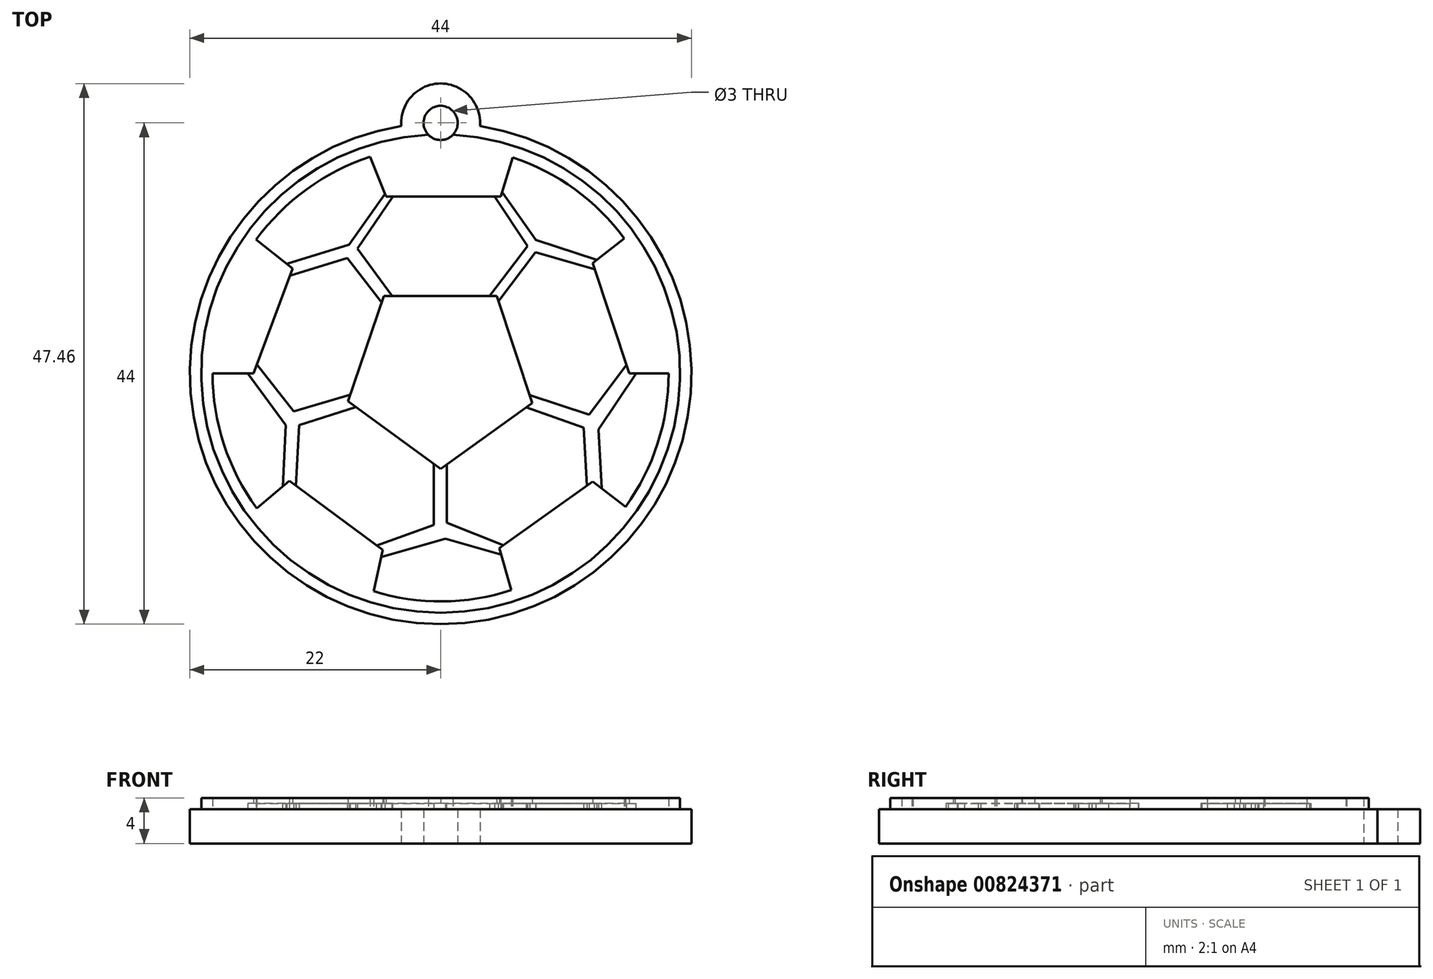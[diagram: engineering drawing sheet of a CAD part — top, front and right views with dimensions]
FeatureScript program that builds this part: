
annotation { "Feature Type Name" : "Feature", "Feature Type Description" : "" }
export const myFeature = defineFeature(function(context is Context, id is Id, definition is map)
    precondition{}
    {
        {
            var Q0;
            Q0=qCreatedBy(makeId("Top.planeOp"),FACE);
            var sketch = newSketch(context, id + "F0", { "sketchPlane" : qUnion([Q0])});
            skArc(sketch, "E0", {"start": v(-3.45, 21.73) * mm, "mid": v(0, -22) * mm, "end": v(3.45, 21.73) * mm});
            skPoint(sketch, "E1.start.orphan", {"position": v(0, -14.87) * mm});
            skCircle(sketch, "E2", {"center": v(0, 22) * mm, "radius": 1.5 * mm});
            skArc(sketch, "E3", {"start": v(3.45, 21.73) * mm, "mid": v(0, 25.46) * mm, "end": v(-3.45, 21.73) * mm});
            skSolve(sketch);
        }
        {
            var Q0;
            Q0=makeQuery(id+"F0.imprint","IMPRINT",FACE,{"disambiguationData":[TD([[makeQuery(id+"F0.imprint","IMPRINT",EDGE,{"derivedFrom":sQuery(id+"F0.wireOp",EDGE,"E0")}),1.0]])]});
            extrude(context, id + "F1", {"entities" : qUnion([Q0]), "depth" : 3 * mm, "offsetDistance" : 25 * mm});
        }
        {
            var Q0;
            Q0=makeQuery(id+"F1.opExtrude","CAP_FACE",FACE,{"disambiguationData":[OSD([sQuery(id+"F0.wireOp",EDGE,"E0")])],"isStart":false});
            var sketch = newSketch(context, id + "F2", { "sketchPlane" : qUnion([Q0])});
            skArc(sketch, "E4", {"start": v(-20, 0) * mm, "mid": v(-19, -6.22) * mm, "end": v(-16.13, -11.83) * mm});
            skLineSegment(sketch, "E5", {"start": v(-6.18, 19.02) * mm, "end": v(-4.8, 15.53) * mm});
            skLineSegment(sketch, "E6", {"start": v(-4.8, 15.53) * mm, "end": v(5.27, 15.53) * mm});
            skLineSegment(sketch, "E7", {"start": v(5.27, 15.53) * mm, "end": v(6.34, 18.97) * mm});
            skLineSegment(sketch, "E8", {"start": v(16.1, 11.85) * mm, "end": v(13.33, 9.69) * mm});
            skLineSegment(sketch, "E9", {"start": v(13.33, 9.69) * mm, "end": v(16.54, 0) * mm});
            skLineSegment(sketch, "E10", {"start": v(16.54, 0) * mm, "end": v(20, 0) * mm});
            skLineSegment(sketch, "E11", {"start": v(-16.18, 11.75) * mm, "end": v(-13, 9.23) * mm});
            skLineSegment(sketch, "E12", {"start": v(-13, 9.23) * mm, "end": v(-16.43, 0) * mm});
            skLineSegment(sketch, "E13", {"start": v(-16.43, 0) * mm, "end": v(-20, 0) * mm});
            skLineSegment(sketch, "E14", {"start": v(-16.13, -11.83) * mm, "end": v(-13.28, -9.43) * mm});
            skLineSegment(sketch, "E15", {"start": v(-13.28, -9.43) * mm, "end": v(-5.1, -15.5) * mm});
            skLineSegment(sketch, "E16", {"start": v(-5.1, -15.5) * mm, "end": v(-5.89, -19.11) * mm});
            skLineSegment(sketch, "E17", {"start": v(6.2, -19.02) * mm, "end": v(5.15, -15.32) * mm});
            skLineSegment(sketch, "E18", {"start": v(5.15, -15.32) * mm, "end": v(13.33, -9.48) * mm});
            skLineSegment(sketch, "E19", {"start": v(13.33, -9.48) * mm, "end": v(16.23, -11.69) * mm});
            skLineSegment(sketch, "E20", {"start": v(-5, 6.8) * mm, "end": v(4.92, 6.8) * mm});
            skLineSegment(sketch, "E21", {"start": v(4.92, 6.8) * mm, "end": v(8.05, -2.58) * mm});
            skLineSegment(sketch, "E22", {"start": v(8.05, -2.58) * mm, "end": v(0, -8.36) * mm});
            skLineSegment(sketch, "E23", {"start": v(0, -8.36) * mm, "end": v(-8.12, -2.44) * mm});
            skLineSegment(sketch, "E24", {"start": v(-8.12, -2.44) * mm, "end": v(-5, 6.8) * mm});
            skCircle(sketch, "E25.0", {"center": v(0, 0) * mm, "radius": 21 * mm});
            skArc(sketch, "E26.trimOffspring", {"start": v(-6.18, 19.02) * mm, "mid": v(-11.76, 16.18) * mm, "end": v(-16.18, 11.75) * mm});
            skArc(sketch, "E27.trimOffspring", {"start": v(16.1, 11.85) * mm, "mid": v(11.77, 16.17) * mm, "end": v(6.34, 18.97) * mm});
            skLineSegment(sketch, "E28.trimOffspring", {"start": v(21, 0) * mm, "end": v(21.06, 0) * mm});
            skArc(sketch, "E29.trimOffspring", {"start": v(16.23, -11.69) * mm, "mid": v(19.03, -6.14) * mm, "end": v(20, 0) * mm});
            skArc(sketch, "E30.trimOffspring", {"start": v(-5.89, -19.11) * mm, "mid": v(0.16, -20) * mm, "end": v(6.2, -19.02) * mm});
            skSolve(sketch);
        }
        {
            var Q0;
            Q0=makeQuery(id+"F2.imprint","IMPRINT",FACE,{"disambiguationData":[TD([[makeQuery(id+"F2.imprint","IMPRINT",EDGE,{"derivedFrom":sQuery(id+"F2.wireOp",EDGE,"E20")}),-1.0]])]});
            var Q1;
            Q1=makeQuery(id+"F2.imprint","IMPRINT",FACE,{"disambiguationData":[TD([[makeQuery(id+"F2.imprint","IMPRINT",EDGE,{"derivedFrom":sQuery(id+"F2.wireOp",EDGE,"E4")}),-1.0]])]});
            extrude(context, id + "F3", {"entities" : qUnion([Q0, Q1]), "depth" : 1 * mm, "offsetDistance" : 25 * mm});
        }
        {
            var Q0;
            Q0=makeQuery(id+"F1.opExtrude","CAP_FACE",FACE,{"disambiguationData":[OSD([sQuery(id+"F0.wireOp",EDGE,"E0")])],"isStart":false});
            var sketch = newSketch(context, id + "F4", { "sketchPlane" : qUnion([Q0])});
            skLineSegment(sketch, "E31", {"start": v(-4.64, 16.12) * mm, "end": v(-8.04, 11.32) * mm});
            skLineSegment(sketch, "E32", {"start": v(-8.04, 11.32) * mm, "end": v(-13.96, 9.48) * mm});
            skLineSegment(sketch, "E33", {"start": v(-13.96, 9.48) * mm, "end": v(-13.3, 8.57) * mm});
            skLineSegment(sketch, "E34", {"start": v(-13.3, 8.57) * mm, "end": v(-8.2, 10.13) * mm});
            skLineSegment(sketch, "E35", {"start": v(-8.2, 10.13) * mm, "end": v(-5.02, 6.01) * mm});
            skLineSegment(sketch, "E36", {"start": v(-5.02, 6.01) * mm, "end": v(-4.17, 6.67) * mm});
            skLineSegment(sketch, "E37", {"start": v(-4.17, 6.67) * mm, "end": v(-7.31, 10.98) * mm});
            skLineSegment(sketch, "E38", {"start": v(-7.31, 10.98) * mm, "end": v(-3.97, 15.86) * mm});
            skLineSegment(sketch, "E39", {"start": v(-3.97, 15.86) * mm, "end": v(-4.64, 16.12) * mm});
            skLineSegment(sketch, "E40", {"start": v(4.5, 15.86) * mm, "end": v(7.62, 11.2) * mm});
            skLineSegment(sketch, "E41", {"start": v(7.62, 11.2) * mm, "end": v(4.16, 6.62) * mm});
            skLineSegment(sketch, "E42", {"start": v(4.16, 6.62) * mm, "end": v(4.87, 6.08) * mm});
            skLineSegment(sketch, "E43", {"start": v(4.87, 6.08) * mm, "end": v(8.33, 10.65) * mm});
            skLineSegment(sketch, "E44", {"start": v(8.33, 10.65) * mm, "end": v(13.91, 9.05) * mm});
            skLineSegment(sketch, "E45", {"start": v(13.91, 9.05) * mm, "end": v(14.13, 9.82) * mm});
            skLineSegment(sketch, "E46", {"start": v(14.13, 9.82) * mm, "end": v(8.36, 11.71) * mm});
            skLineSegment(sketch, "E47", {"start": v(8.36, 11.71) * mm, "end": v(5.13, 16.3) * mm});
            skLineSegment(sketch, "E48", {"start": v(5.13, 16.3) * mm, "end": v(4.5, 15.86) * mm});
            skLineSegment(sketch, "E49", {"start": v(7.27, -1.7) * mm, "end": v(6.98, -2.76) * mm});
            skLineSegment(sketch, "E50", {"start": v(6.98, -2.76) * mm, "end": v(12.56, -4.76) * mm});
            skLineSegment(sketch, "E51", {"start": v(12.56, -4.76) * mm, "end": v(12.88, -10.51) * mm});
            skLineSegment(sketch, "E52", {"start": v(12.88, -10.51) * mm, "end": v(14.16, -10.44) * mm});
            skLineSegment(sketch, "E53", {"start": v(14.16, -10.44) * mm, "end": v(13.85, -4.9) * mm});
            skLineSegment(sketch, "E54", {"start": v(13.85, -4.9) * mm, "end": v(17.51, 0.53) * mm});
            skLineSegment(sketch, "E55", {"start": v(17.51, 0.53) * mm, "end": v(16.6, 1.14) * mm});
            skLineSegment(sketch, "E56", {"start": v(16.6, 1.14) * mm, "end": v(13.02, -3.6) * mm});
            skLineSegment(sketch, "E57", {"start": v(13.02, -3.6) * mm, "end": v(7.27, -1.7) * mm});
            skLineSegment(sketch, "E58", {"start": v(-0.6, -7.1) * mm, "end": v(0.54, -7.1) * mm});
            skLineSegment(sketch, "E59", {"start": v(0.54, -7.1) * mm, "end": v(0.54, -13.1) * mm});
            skLineSegment(sketch, "E60", {"start": v(0.54, -13.1) * mm, "end": v(6.18, -15.35) * mm});
            skLineSegment(sketch, "E61", {"start": v(6.18, -15.35) * mm, "end": v(5.9, -16.07) * mm});
            skLineSegment(sketch, "E62", {"start": v(5.9, -16.07) * mm, "end": v(0.43, -14.5) * mm});
            skLineSegment(sketch, "E63", {"start": v(0.43, -14.5) * mm, "end": v(-5.67, -16.24) * mm});
            skLineSegment(sketch, "E64", {"start": v(-5.67, -16.24) * mm, "end": v(-5.96, -15.23) * mm});
            skLineSegment(sketch, "E65", {"start": v(-5.96, -15.23) * mm, "end": v(-0.6, -13.3) * mm});
            skLineSegment(sketch, "E66", {"start": v(-0.6, -13.3) * mm, "end": v(-0.6, -7.1) * mm});
            skLineSegment(sketch, "E67", {"start": v(-17.4, 0.65) * mm, "end": v(-16.37, 1.11) * mm});
            skLineSegment(sketch, "E68", {"start": v(-16.37, 1.11) * mm, "end": v(-12.88, -3.32) * mm});
            skLineSegment(sketch, "E69", {"start": v(-12.88, -3.32) * mm, "end": v(-7.37, -1.7) * mm});
            skLineSegment(sketch, "E70", {"start": v(-7.37, -1.7) * mm, "end": v(-6.82, -2.76) * mm});
            skLineSegment(sketch, "E71", {"start": v(-6.82, -2.76) * mm, "end": v(-12.43, -4.52) * mm});
            skLineSegment(sketch, "E72", {"start": v(-12.43, -4.52) * mm, "end": v(-12.72, -10.32) * mm});
            skLineSegment(sketch, "E73", {"start": v(-12.72, -10.32) * mm, "end": v(-13.87, -10.26) * mm});
            skLineSegment(sketch, "E74", {"start": v(-13.87, -10.26) * mm, "end": v(-13.59, -4.52) * mm});
            skLineSegment(sketch, "E75", {"start": v(-13.59, -4.52) * mm, "end": v(-17.4, 0.65) * mm});
            skSolve(sketch);
        }
        {
            var Q0;
            Q0 = qSketchRegion(id + "F4", true);
            extrude(context, id + "F5", {"entities" : qUnion([Q0]), "operationType" : NewBodyOperationType.ADD, "depth" : 0.5 * mm, "offsetDistance" : 25 * mm});
        }
    });
